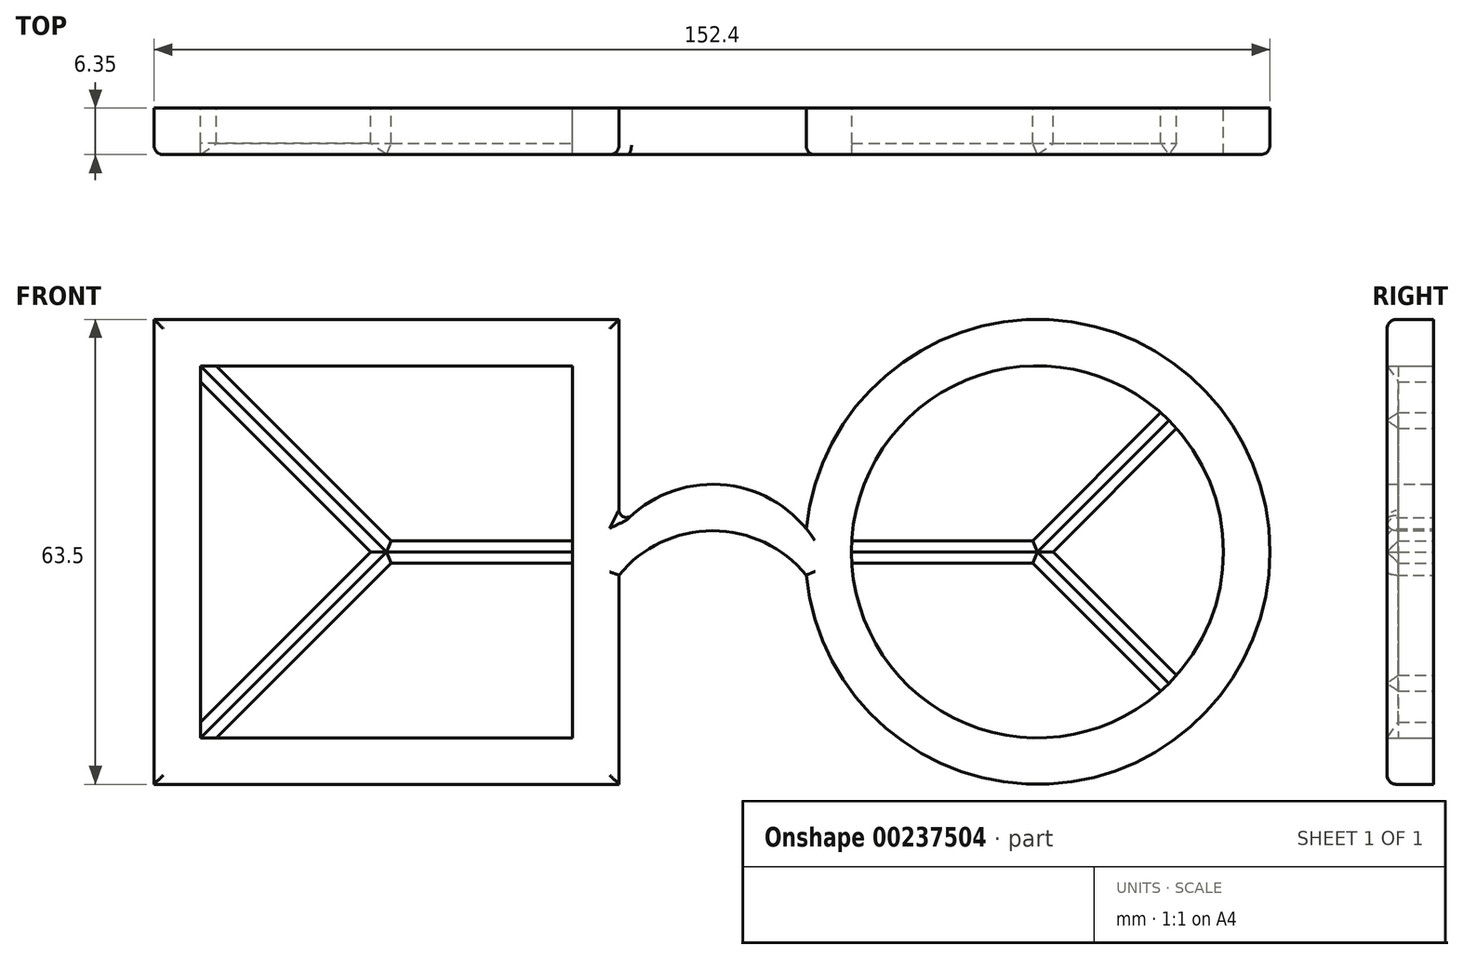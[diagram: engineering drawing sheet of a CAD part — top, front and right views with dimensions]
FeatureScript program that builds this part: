
annotation { "Feature Type Name" : "Feature", "Feature Type Description" : "" }
export const myFeature = defineFeature(function(context is Context, id is Id, definition is map)
    precondition{}
    {
        {
            var Q0;
            Q0=qCreatedBy(makeId("Front.planeOp"),FACE);
            var sketch = newSketch(context, id + "F0", { "sketchPlane" : qUnion([Q0])});
            skArc(sketch, "E0", {"start": v(19.1, -1.52) * mm, "mid": v(34.73, -23.47) * mm, "end": v(61.3, -19) * mm});
            skCircle(sketch, "E1.0", {"center": v(44.45, 0) * mm, "radius": 31.75 * mm});
            skLineSegment(sketch, "E2", {"start": v(44.45, 0) * mm, "end": v(19.05, 0) * mm, "construction": true});
            skLineSegment(sketch, "E3", {"start": v(44.45, 0) * mm, "end": v(62.41, 17.96) * mm, "construction": true});
            skLineSegment(sketch, "E4", {"start": v(44.45, 0) * mm, "end": v(62.41, -17.96) * mm, "construction": true});
            skLineSegment(sketch, "E5.0", {"start": v(46.6, 0) * mm, "end": v(63.46, 16.85) * mm});
            skLineSegment(sketch, "E5.1", {"start": v(46.6, 0) * mm, "end": v(63.46, -16.85) * mm});
            skLineSegment(sketch, "E6.0", {"start": v(43.82, 1.52) * mm, "end": v(61.3, 19) * mm});
            skLineSegment(sketch, "E6.1", {"start": v(43.82, -1.52) * mm, "end": v(61.3, -19) * mm});
            skLineSegment(sketch, "E7.0", {"start": v(43.82, 1.52) * mm, "end": v(19.1, 1.52) * mm});
            skLineSegment(sketch, "E8.0", {"start": v(43.82, -1.52) * mm, "end": v(19.1, -1.52) * mm});
            skArc(sketch, "E9.trimOffspring", {"start": v(61.3, 19) * mm, "mid": v(34.73, 23.47) * mm, "end": v(19.1, 1.52) * mm});
            skArc(sketch, "E10.trimOffspring", {"start": v(63.46, -16.85) * mm, "mid": v(69.85, 0) * mm, "end": v(63.46, 16.85) * mm});
            skSolve(sketch);
        }
        {
            var Q0;
            Q0=makeQuery(id+"F0.imprint","IMPRINT",FACE,{"disambiguationData":[TD([[makeQuery(id+"F0.imprint","IMPRINT",EDGE,{"derivedFrom":sQuery(id+"F0.wireOp",EDGE,"E0")}),-1.0]])]});
            extrude(context, id + "F1", {"entities" : qUnion([Q0]), "depth" : 6.35 * mm});
        }
        {
            var Q0;
            Q0=qCreatedBy(makeId("Front.planeOp"),FACE);
            var sketch = newSketch(context, id + "F2", { "sketchPlane" : qUnion([Q0])});
            skLineSegment(sketch, "E11.bottom", {"start": v(-12.7, 31.75) * mm, "end": v(-76.2, 31.75) * mm});
            skLineSegment(sketch, "E11.top", {"start": v(-12.7, -31.75) * mm, "end": v(-76.2, -31.75) * mm});
            skLineSegment(sketch, "E11.left", {"start": v(-12.7, 31.75) * mm, "end": v(-12.7, -31.75) * mm});
            skLineSegment(sketch, "E11.right", {"start": v(-76.2, 31.75) * mm, "end": v(-76.2, -31.75) * mm});
            skPoint(sketch, "E11.middle", {"position": v(-44.45, 0) * mm});
            skLineSegment(sketch, "E12", {"start": v(-12.7, 31.75) * mm, "end": v(44.45, 31.75) * mm, "construction": true});
            skLineSegment(sketch, "E13", {"start": v(-12.7, 0) * mm, "end": v(0, 0) * mm, "construction": true});
            skLineSegment(sketch, "E14", {"start": v(0, 0) * mm, "end": v(12.7, 0) * mm, "construction": true});
            skLineSegment(sketch, "E15", {"start": v(44.45, 31.75) * mm, "end": v(44.45, 0) * mm, "construction": true});
            skLineSegment(sketch, "E16", {"start": v(12.7, 0) * mm, "end": v(76.2, 0) * mm, "construction": true});
            skLineSegment(sketch, "E17", {"start": v(-44.45, 0) * mm, "end": v(-19.05, 0) * mm, "construction": true});
            skLineSegment(sketch, "E18", {"start": v(-44.45, 0) * mm, "end": v(-69.85, 25.4) * mm, "construction": true});
            skLineSegment(sketch, "E19", {"start": v(-44.45, 0) * mm, "end": v(-69.85, -25.4) * mm, "construction": true});
            skLineSegment(sketch, "E20.0", {"start": v(-46.6, 0) * mm, "end": v(-69.85, 23.24) * mm});
            skLineSegment(sketch, "E20.1", {"start": v(-46.6, 0) * mm, "end": v(-69.85, -23.24) * mm});
            skLineSegment(sketch, "E21.0", {"start": v(-43.82, 1.52) * mm, "end": v(-67.7, 25.4) * mm});
            skLineSegment(sketch, "E21.1", {"start": v(-43.82, -1.52) * mm, "end": v(-67.7, -25.4) * mm});
            skLineSegment(sketch, "E22.0", {"start": v(-43.82, -1.52) * mm, "end": v(-19.05, -1.52) * mm});
            skLineSegment(sketch, "E23.0", {"start": v(-43.82, 1.52) * mm, "end": v(-19.05, 1.52) * mm});
            skLineSegment(sketch, "E24.0", {"start": v(-19.05, 25.4) * mm, "end": v(-67.7, 25.4) * mm});
            skLineSegment(sketch, "E24.1", {"start": v(-19.05, 25.4) * mm, "end": v(-19.05, 1.52) * mm});
            skLineSegment(sketch, "E24.2", {"start": v(-19.05, -25.4) * mm, "end": v(-67.7, -25.4) * mm});
            skLineSegment(sketch, "E24.3", {"start": v(-69.85, 23.24) * mm, "end": v(-69.85, -23.24) * mm});
            skLineSegment(sketch, "E25.trimOffspring", {"start": v(-19.05, -1.52) * mm, "end": v(-19.05, -25.4) * mm});
            skSolve(sketch);
        }
        {
            var Q0;
            Q0=makeQuery(id+"F2.imprint","IMPRINT",FACE,{"disambiguationData":[TD([[makeQuery(id+"F2.imprint","IMPRINT",EDGE,{"derivedFrom":sQuery(id+"F2.wireOp",EDGE,"E11.bottom")}),1.0]])]});
            extrude(context, id + "F3", {"entities" : qUnion([Q0]), "depth" : 6.35 * mm});
        }
        {
            var Q0;
            Q0=qCreatedBy(makeId("Front.planeOp"),FACE);
            var sketch = newSketch(context, id + "F4", { "sketchPlane" : qUnion([Q0])});
            skArc(sketch, "E26", {"start": v(12.86, 3.17) * mm, "mid": v(0.08, 9.23) * mm, "end": v(-12.7, 3.17) * mm});
            skLineSegment(sketch, "E27", {"start": v(-12.7, 3.18) * mm, "end": v(12.86, 3.18) * mm, "construction": true});
            skLineSegment(sketch, "E28.0", {"start": v(-12.7, -3.18) * mm, "end": v(12.86, -3.18) * mm, "construction": true});
            skArc(sketch, "E29", {"start": v(12.86, -3.17) * mm, "mid": v(0.08, 2.88) * mm, "end": v(-12.7, -3.18) * mm});
            skLineSegment(sketch, "E30", {"start": v(-12.7, -3.17) * mm, "end": v(0.08, -13.63) * mm, "construction": true});
            skLineSegment(sketch, "E31", {"start": v(-12.7, 3.17) * mm, "end": v(0.08, -7.28) * mm, "construction": true});
            skLineSegment(sketch, "E32", {"start": v(0, -3.18) * mm, "end": v(0, 3.18) * mm, "construction": true});
            skLineSegment(sketch, "E33", {"start": v(-12.7, -3.17) * mm, "end": v(-12.7, 3.17) * mm});
            skArc(sketch, "E34", {"start": v(12.86, 3.17) * mm, "mid": v(12.77, 0) * mm, "end": v(12.86, -3.17) * mm});
            skLineSegment(sketch, "E35", {"start": v(69.92, 0) * mm, "end": v(12.86, 3.17) * mm, "construction": true});
            skSolve(sketch);
        }
        {
            var Q0;
            Q0=makeQuery(id+"F4.imprint","IMPRINT",FACE,{"disambiguationData":[TD([[makeQuery(id+"F4.imprint","IMPRINT",EDGE,{"derivedFrom":sQuery(id+"F4.wireOp",EDGE,"E26")}),1.0]])]});
            extrude(context, id + "F5", {"entities" : qUnion([Q0]), "operationType" : NewBodyOperationType.ADD, "depth" : 6.35 * mm});
        }
        {
            var Q0;
            Q0=makeQuery(id+"F3.opExtrude","CAP_EDGE",EDGE,{"disambiguationData":[OSD([sQuery(id+"F2.wireOp",EDGE,"E20.0")])],"isStart":false});
            var Q1;
            Q1=makeQuery(id+"F3.opExtrude","CAP_EDGE",EDGE,{"disambiguationData":[OSD([sQuery(id+"F2.wireOp",EDGE,"E21.0")])],"isStart":false});
            var Q2;
            Q2=makeQuery(id+"F3.opExtrude","CAP_EDGE",EDGE,{"disambiguationData":[OSD([sQuery(id+"F2.wireOp",EDGE,"E23.0")])],"isStart":false});
            var Q3;
            Q3=makeQuery(id+"F3.opExtrude","CAP_EDGE",EDGE,{"disambiguationData":[OSD([sQuery(id+"F2.wireOp",EDGE,"E22.0")])],"isStart":false});
            var Q4;
            Q4=makeQuery(id+"F3.opExtrude","CAP_EDGE",EDGE,{"disambiguationData":[OSD([sQuery(id+"F2.wireOp",EDGE,"E21.1")])],"isStart":false});
            var Q5;
            Q5=makeQuery(id+"F3.opExtrude","CAP_EDGE",EDGE,{"disambiguationData":[OSD([sQuery(id+"F2.wireOp",EDGE,"E20.1")])],"isStart":false});
            var Q6;
            Q6=makeQuery(id+"F1.opExtrude","CAP_EDGE",EDGE,{"disambiguationData":[OSD([sQuery(id+"F0.wireOp",EDGE,"E7.0")])],"isStart":false});
            var Q7;
            Q7=makeQuery(id+"F1.opExtrude","CAP_EDGE",EDGE,{"disambiguationData":[OSD([sQuery(id+"F0.wireOp",EDGE,"E6.0")])],"isStart":false});
            var Q8;
            Q8=makeQuery(id+"F1.opExtrude","CAP_EDGE",EDGE,{"disambiguationData":[OSD([sQuery(id+"F0.wireOp",EDGE,"E5.0")])],"isStart":false});
            var Q9;
            Q9=makeQuery(id+"F1.opExtrude","CAP_EDGE",EDGE,{"disambiguationData":[OSD([sQuery(id+"F0.wireOp",EDGE,"E5.1")])],"isStart":false});
            var Q10;
            Q10=makeQuery(id+"F1.opExtrude","CAP_EDGE",EDGE,{"disambiguationData":[OSD([sQuery(id+"F0.wireOp",EDGE,"E6.1")])],"isStart":false});
            var Q11;
            Q11=makeQuery(id+"F1.opExtrude","CAP_EDGE",EDGE,{"disambiguationData":[OSD([sQuery(id+"F0.wireOp",EDGE,"E8.0")])],"isStart":false});
            chamfer(context, id + "F6", {"entities" : qUnion([Q0, Q1, Q2, Q3, Q4, Q5, Q6, Q7, Q8, Q9, Q10, Q11]), "width" : 1.52 * mm, "tangentPropagation" : true});
        }
        {
            var Q0;
            Q0=makeQuery(id+"F3.opExtrude","CAP_EDGE",EDGE,{"disambiguationData":[OSD([sQuery(id+"F2.wireOp",EDGE,"E11.bottom")])],"isStart":false});
            var Q1;
            Q1=makeQuery(id+"F3.opExtrude","CAP_EDGE",EDGE,{"disambiguationData":[OSD([sQuery(id+"F2.wireOp",EDGE,"E11.right")])],"isStart":false});
            var Q2;
            Q2=makeQuery(id+"F3.opExtrude","CAP_EDGE",EDGE,{"disambiguationData":[OSD([sQuery(id+"F2.wireOp",EDGE,"E11.top")])],"isStart":false});
            var Q3;
            {var subQ0=sQuery(id+"F2.wireOp",EDGE,"E11.left");var subQ1=sQuery(id+"F2.wireOp",EDGE,"E11.top");Q3=makeQuery(id+"F5.boolean.opBoolean","SPLIT",EDGE,{"disambiguationData":[TD([makeQuery(id+"F3.opExtrude","SWEPT_FACE",FACE,{"disambiguationData":[OSD([subQ1])]})])],"derivedFrom":makeQuery(id+"F3.opExtrude","CAP_EDGE",EDGE,{"disambiguationData":[OSD([subQ0])],"isStart":false})});}
            var Q4;
            {var subQ0=sQuery(id+"F2.wireOp",EDGE,"E11.left");var subQ1=sQuery(id+"F2.wireOp",EDGE,"E11.bottom");Q4=makeQuery(id+"F5.boolean.opBoolean","SPLIT",EDGE,{"disambiguationData":[TD([makeQuery(id+"F3.opExtrude","SWEPT_FACE",FACE,{"disambiguationData":[OSD([subQ1])]})])],"derivedFrom":makeQuery(id+"F3.opExtrude","CAP_EDGE",EDGE,{"disambiguationData":[OSD([subQ0])],"isStart":false})});}
            var Q5;
            Q5=makeQuery(id+"F5.opExtrude","CAP_EDGE",EDGE,{"disambiguationData":[OSD([sQuery(id+"F4.wireOp",EDGE,"E29")])],"isStart":false});
            var Q6;
            Q6=makeQuery(id+"F1.opExtrude","CAP_EDGE",EDGE,{"disambiguationData":[OSD([sQuery(id+"F0.wireOp",EDGE,"E1.0")])],"isStart":false});
            fillet(context, id + "F7", {"entities" : qUnion([Q0, Q1, Q2, Q3, Q4, Q5, Q6]), "radius" : 1.27 * mm, "tangentPropagation" : true, "allowEdgeOverflow" : false});
        }
        {
            var Q0;
            Q0=makeQuery(id+"F5.opExtrude","SWEPT_EDGE",EDGE,{"disambiguationData":[OSD([sQuery(id+"F4.wireOp",EDGE,"E26"),sQuery(id+"F4.wireOp",EDGE,"E33")])]});
            var Q1;
            Q1=makeQuery(id+"F5.opExtrude","SWEPT_EDGE",EDGE,{"disambiguationData":[OSD([sQuery(id+"F4.wireOp",EDGE,"E26"),sQuery(id+"F4.wireOp",EDGE,"E34")])]});
            fillet(context, id + "F8", {"entities" : qUnion([Q0, Q1]), "radius" : 1.02 * mm, "tangentPropagation" : true, "allowEdgeOverflow" : false});
        }
    });
